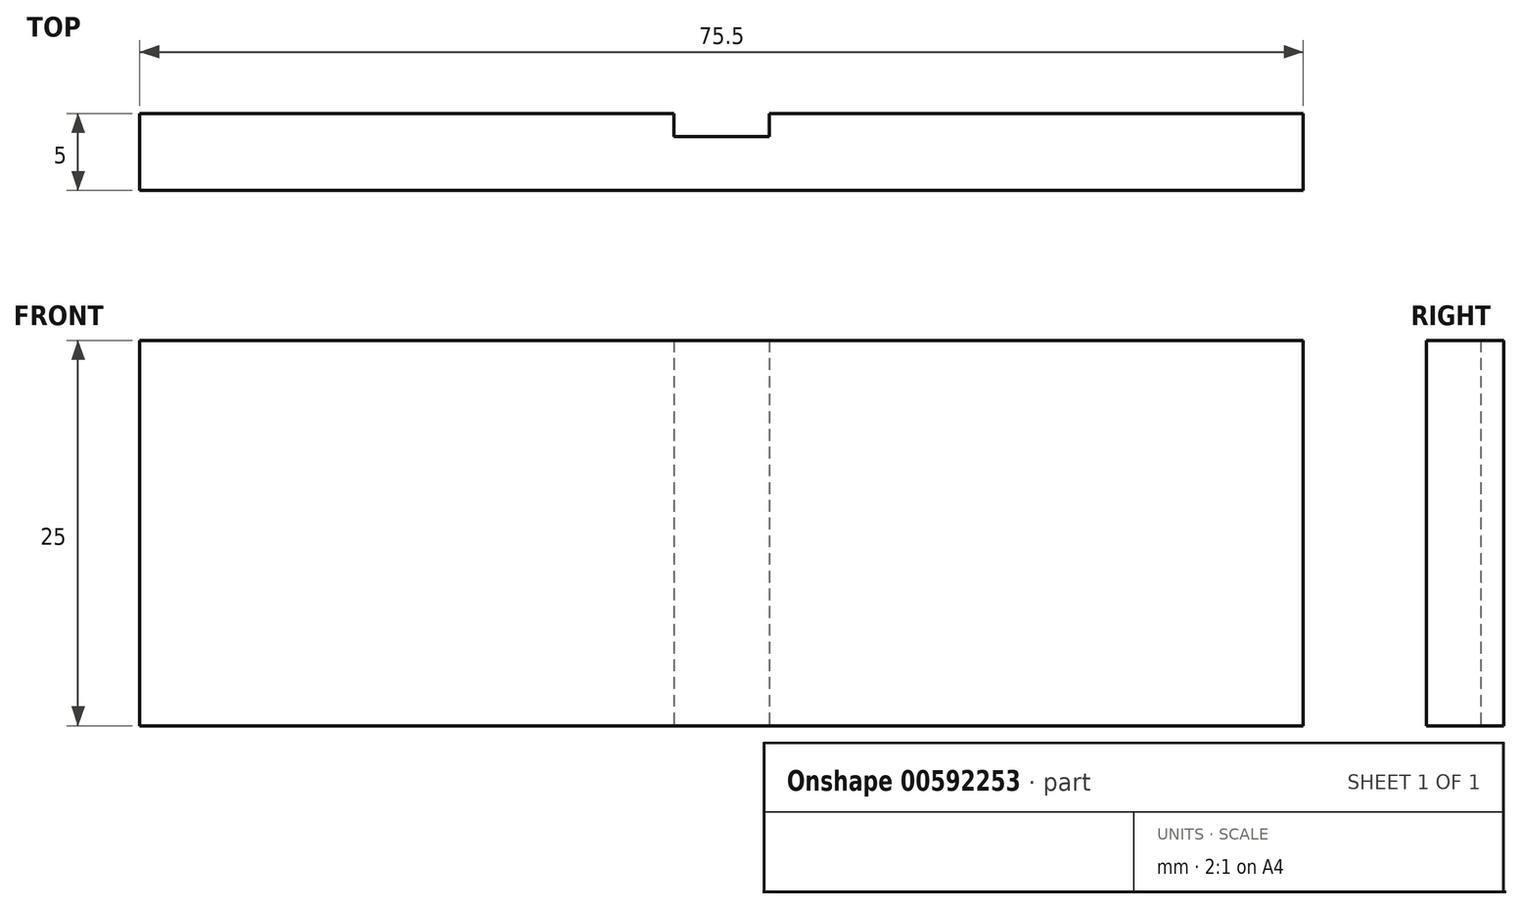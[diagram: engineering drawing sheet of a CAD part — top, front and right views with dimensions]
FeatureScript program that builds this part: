
annotation { "Feature Type Name" : "Feature", "Feature Type Description" : "" }
export const myFeature = defineFeature(function(context is Context, id is Id, definition is map)
    precondition{}
    {
        {
            var Q0;
            Q0=qCreatedBy(makeId("Top.planeOp"),FACE);
            var sketch = newSketch(context, id + "F0", { "sketchPlane" : qUnion([Q0])});
            skLineSegment(sketch, "E0", {"start": v(-37.75, 0) * mm, "end": v(37.75, 0) * mm});
            skLineSegment(sketch, "E1", {"start": v(37.75, 0) * mm, "end": v(37.75, 5) * mm});
            skLineSegment(sketch, "E2", {"start": v(37.75, 5) * mm, "end": v(3.1, 5) * mm});
            skLineSegment(sketch, "E3", {"start": v(3.1, 5) * mm, "end": v(3.1, 3.5) * mm});
            skLineSegment(sketch, "E4", {"start": v(3.1, 3.5) * mm, "end": v(-3.1, 3.5) * mm});
            skLineSegment(sketch, "E5", {"start": v(-3.1, 3.5) * mm, "end": v(-3.1, 5) * mm});
            skLineSegment(sketch, "E6", {"start": v(-3.1, 5) * mm, "end": v(-37.75, 5) * mm});
            skLineSegment(sketch, "E7", {"start": v(-37.75, 5) * mm, "end": v(-37.75, 0) * mm});
            skSolve(sketch);
        }
        {
            var Q0;
            Q0=makeQuery(id+"F0.imprint","IMPRINT",FACE,{"disambiguationData":[TD([[makeQuery(id+"F0.imprint","IMPRINT",EDGE,{"derivedFrom":sQuery(id+"F0.wireOp",EDGE,"E0")}),1.0]])]});
            extrude(context, id + "F1", {"entities" : qUnion([Q0]), "depth" : 25 * mm, "offsetDistance" : 25 * mm});
        }
    });
